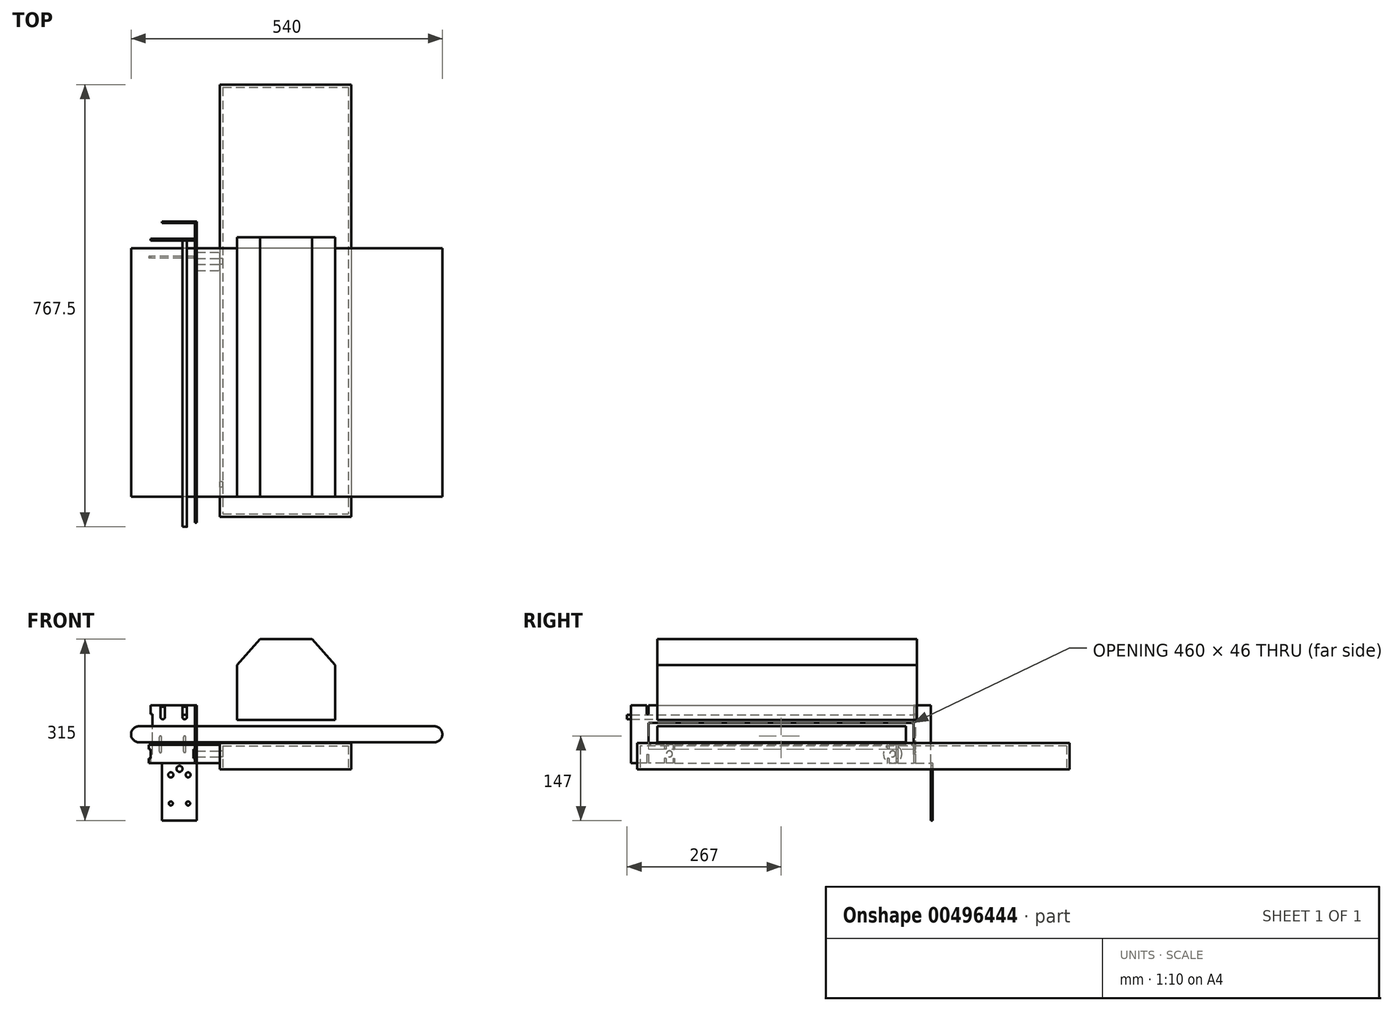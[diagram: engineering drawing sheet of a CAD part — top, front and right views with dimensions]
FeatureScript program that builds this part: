
annotation { "Feature Type Name" : "Feature", "Feature Type Description" : "" }
export const myFeature = defineFeature(function(context is Context, id is Id, definition is map)
    precondition{}
    {
        {
            var Q0;
            Q0=qCreatedBy(makeId("Front.planeOp"),FACE);
            var sketch = newSketch(context, id + "F0", { "sketchPlane" : qUnion([Q0])});
            skLineSegment(sketch, "E0.bottom", {"start": v(270, -14) * mm, "end": v(-270, -14) * mm});
            skLineSegment(sketch, "E0.top", {"start": v(270, 14) * mm, "end": v(-270, 14) * mm});
            skLineSegment(sketch, "E0.left", {"start": v(270, -14) * mm, "end": v(270, 14) * mm});
            skLineSegment(sketch, "E0.right", {"start": v(-270, -14) * mm, "end": v(-270, 14) * mm});
            skPoint(sketch, "E0.middle", {"position": v(0, 0) * mm});
            skSolve(sketch);
        }
        {
            var Q0;
            Q0 = qSketchRegion(id + "F0", true);
            extrude(context, id + "F1", {"entities" : qUnion([Q0]), "oppositeDirection" : true, "depth" : 431 * mm});
        }
        {
            var Q0;
            Q0=makeQuery(id+"F1.opExtrude","SWEPT_EDGE",EDGE,{"disambiguationData":[OSD([sQuery(id+"F0.wireOp",EDGE,"E0.top"),sQuery(id+"F0.wireOp",EDGE,"E0.right")])]});
            var Q1;
            Q1=makeQuery(id+"F1.opExtrude","SWEPT_EDGE",EDGE,{"disambiguationData":[OSD([sQuery(id+"F0.wireOp",EDGE,"E0.bottom"),sQuery(id+"F0.wireOp",EDGE,"E0.right")])]});
            var Q2;
            Q2=makeQuery(id+"F1.opExtrude","SWEPT_EDGE",EDGE,{"disambiguationData":[OSD([sQuery(id+"F0.wireOp",EDGE,"E0.top"),sQuery(id+"F0.wireOp",EDGE,"E0.left")])]});
            var Q3;
            Q3=makeQuery(id+"F1.opExtrude","SWEPT_EDGE",EDGE,{"disambiguationData":[OSD([sQuery(id+"F0.wireOp",EDGE,"E0.bottom"),sQuery(id+"F0.wireOp",EDGE,"E0.left")])]});
            fillet(context, id + "F2", {"entities" : qUnion([Q0, Q1, Q2, Q3]), "radius" : 14 * mm, "tangentPropagation" : true, "allowEdgeOverflow" : false});
        }
        {
            var Q0;
            Q0=makeQuery(id+"F1.opExtrude","CAP_FACE",FACE,{"disambiguationData":[OSD([sQuery(id+"F0.wireOp",EDGE,"E0.bottom"),sQuery(id+"F0.wireOp",EDGE,"E0.top"),sQuery(id+"F0.wireOp",EDGE,"E0.left"),sQuery(id+"F0.wireOp",EDGE,"E0.right")])],"isStart":true});
            var sketch = newSketch(context, id + "F3", { "sketchPlane" : qUnion([Q0])});
            skLineSegment(sketch, "E1.bottom", {"start": v(-116, -15) * mm, "end": v(112, -15) * mm});
            skLineSegment(sketch, "E1.top", {"start": v(-116, -61) * mm, "end": v(112, -61) * mm});
            skLineSegment(sketch, "E1.left", {"start": v(-116, -15) * mm, "end": v(-116, -61) * mm});
            skLineSegment(sketch, "E1.right", {"start": v(112, -15) * mm, "end": v(112, -61) * mm});
            skSolve(sketch);
        }
        {
            var Q0;
            Q0 = qSketchRegion(id + "F3", true);
            extrude(context, id + "F4", {"entities" : qUnion([Q0]), "oppositeDirection" : true, "depth" : 715 * mm, "hasSecondDirection" : true, "secondDirectionOppositeDirection" : false, "secondDirectionDepth" : 35 * mm});
        }
        {
            var Q0;
            Q0=qCreatedBy(makeId("Front.planeOp"),FACE);
            var sketch = newSketch(context, id + "F5", { "sketchPlane" : qUnion([Q0])});
            skLineSegment(sketch, "E2.bottom", {"start": v(-46.31, 165) * mm, "end": v(44.31, 165) * mm});
            skLineSegment(sketch, "E2.top", {"start": v(-86, 25) * mm, "end": v(84, 25) * mm});
            skLineSegment(sketch, "E2.left", {"start": v(-86, 120) * mm, "end": v(-86, 25) * mm});
            skLineSegment(sketch, "E2.right", {"start": v(84, 120) * mm, "end": v(84, 25) * mm});
            skLineSegment(sketch, "E3", {"start": v(-86, 120) * mm, "end": v(-46.31, 165) * mm});
            skLineSegment(sketch, "E4", {"start": v(44.31, 165) * mm, "end": v(84, 120) * mm});
            skPoint(sketch, "E5.orphan", {"position": v(84, 165) * mm});
            skSolve(sketch);
        }
        {
            var Q0;
            Q0 = qSketchRegion(id + "F5", true);
            extrude(context, id + "F6", {"entities" : qUnion([Q0]), "oppositeDirection" : true, "depth" : 450 * mm});
        }
        {
            var Q0;
            Q0=makeQuery(id+"F1.opExtrude","CAP_FACE",FACE,{"disambiguationData":[OSD([sQuery(id+"F0.wireOp",EDGE,"E0.bottom"),sQuery(id+"F0.wireOp",EDGE,"E0.top"),sQuery(id+"F0.wireOp",EDGE,"E0.left"),sQuery(id+"F0.wireOp",EDGE,"E0.right")])],"isStart":true});
            var sketch = newSketch(context, id + "F7", { "sketchPlane" : qUnion([Q0])});
            skCircle(sketch, "E6", {"center": v(-112.05, 32.23) * mm, "radius": 12.5 * mm});
            skCircle(sketch, "E7", {"center": v(-112.05, 32.23) * mm, "radius": 6 * mm});
            skSolve(sketch);
        }
        {
            var Q0;
            Q0=makeQuery(id+"F7.imprint","IMPRINT",FACE,{"disambiguationData":[TD([[makeQuery(id+"F7.imprint","IMPRINT",EDGE,{"derivedFrom":sQuery(id+"F7.wireOp",EDGE,"E6")}),1.0]])]});
            extrude(context, id + "F8", {"entities" : qUnion([Q0]), "oppositeDirection" : true, "depth" : 400 * mm});
        }
        {
            var Q0;
            Q0=makeQuery(id+"F4.opExtrude","SWEPT_FACE",FACE,{"disambiguationData":[OSD([sQuery(id+"F3.wireOp",EDGE,"E1.top")])]});
            shell(context, id + "F9", {"entities" : qUnion([Q0]), "thickness" : 5 * mm});
        }
        {
            var Q0;
            Q0=makeQuery(id+"F4.opExtrude","SWEPT_FACE",FACE,{"disambiguationData":[OSD([sQuery(id+"F3.wireOp",EDGE,"E1.left")])]});
            var sketch = newSketch(context, id + "F10", { "sketchPlane" : qUnion([Q0])});
            skCircle(sketch, "E8", {"center": v(-21, -34) * mm, "radius": 5 * mm});
            skCircle(sketch, "E9", {"center": v(-408, -34) * mm, "radius": 5 * mm});
            skSolve(sketch);
        }
        {
            var Q0;
            Q0 = qSketchRegion(id + "F10", true);
            var Q1;
            Q1=sQuery(id+"F10.wireOp",EDGE,"E8");
            extrude(context, id + "F11", {"entities" : qUnion([Q0]), "operationType" : NewBodyOperationType.REMOVE, "surfaceEntities" : qUnion([Q1]), "oppositeDirection" : true, "depth" : 5 * mm});
        }
        {
            var Q0;
            Q0=makeQuery(id+"F4.opExtrude","SWEPT_FACE",FACE,{"disambiguationData":[OSD([sQuery(id+"F3.wireOp",EDGE,"E1.left")])]});
            var sketch = newSketch(context, id + "F12", { "sketchPlane" : qUnion([Q0])});
            skCircle(sketch, "E10", {"center": v(-408, -34) * mm, "radius": 16 * mm});
            skCircle(sketch, "E11", {"center": v(-408, -34) * mm, "radius": 5 * mm});
            skSolve(sketch);
        }
        {
            var Q0;
            Q0 = qSketchRegion(id + "F12", true);
            extrude(context, id + "F13", {"entities" : qUnion([Q0]), "depth" : 40 * mm});
        }
        {
            var Q0;
            Q0=makeQuery(id+"F13.opExtrude","CAP_FACE",FACE,{"disambiguationData":[OSD([sQuery(id+"F12.wireOp",EDGE,"E10"),sQuery(id+"F12.wireOp",EDGE,"E11")])],"isStart":false});
            var sketch = newSketch(context, id + "F14", { "sketchPlane" : qUnion([Q0])});
            skLineSegment(sketch, "E12.bottom", {"start": v(-214.5, -18) * mm, "end": v(-30, -18) * mm});
            skLineSegment(sketch, "E12.top", {"start": v(-214.5, -50) * mm, "end": v(-30, -50) * mm});
            skLineSegment(sketch, "E12.right", {"start": v(-21, -18) * mm, "end": v(-21, -50) * mm, "construction": true});
            skLineSegment(sketch, "E13", {"start": v(-214.5, -34) * mm, "end": v(-21, -34) * mm, "construction": true});
            skLineSegment(sketch, "E14", {"start": v(45.55, -50) * mm, "end": v(45.55, 50) * mm});
            skLineSegment(sketch, "E15", {"start": v(15.5, 20) * mm, "end": v(15.5, -18) * mm});
            skLineSegment(sketch, "E16", {"start": v(-214.5, -50) * mm, "end": v(-214.5, -18) * mm, "construction": true});
            skPoint(sketch, "E16.endSnap0", {"position": v(-198.32, -18) * mm});
            skPoint(sketch, "E17.orphan", {"position": v(-214.5, -34) * mm});
            skPoint(sketch, "E18.orphan", {"position": v(-408, -34) * mm});
            skLineSegment(sketch, "E19.MirrorCS", {"start": v(-444.5, 20) * mm, "end": v(-444.5, -18) * mm});
            skLineSegment(sketch, "E20.MirrorCS", {"start": v(-474.55, -50) * mm, "end": v(-474.55, 50) * mm});
            skLineSegment(sketch, "E21.MirrorCS", {"start": v(-214.5, -50) * mm, "end": v(-399, -50) * mm});
            skLineSegment(sketch, "E22.MirrorCS", {"start": v(-214.5, -18) * mm, "end": v(-399, -18) * mm});
            skCircle(sketch, "E23", {"center": v(-408, -34) * mm, "radius": 5.25 * mm});
            skCircle(sketch, "E24", {"center": v(-21, -34) * mm, "radius": 5.25 * mm});
            skLineSegment(sketch, "E25", {"start": v(45.55, 50) * mm, "end": v(18.55, 50) * mm});
            skLineSegment(sketch, "E26", {"start": v(-444.5, 20) * mm, "end": v(15.5, 20) * mm});
            skLineSegment(sketch, "E27.top", {"start": v(-447.55, 35) * mm, "end": v(-444.5, 35) * mm});
            skLineSegment(sketch, "E27.left", {"start": v(-447.55, 50) * mm, "end": v(-447.55, 35) * mm});
            skLineSegment(sketch, "E27.right", {"start": v(-444.5, 50) * mm, "end": v(-444.5, 35) * mm});
            skLineSegment(sketch, "E28.trimOffspring", {"start": v(-447.55, 50) * mm, "end": v(-474.55, 50) * mm});
            skLineSegment(sketch, "E29.top", {"start": v(15.5, 35) * mm, "end": v(18.55, 35) * mm});
            skLineSegment(sketch, "E29.left", {"start": v(15.5, 50) * mm, "end": v(15.5, 35) * mm});
            skLineSegment(sketch, "E29.right", {"start": v(18.55, 50) * mm, "end": v(18.55, 35) * mm});
            skLineSegment(sketch, "E30.trimOffspring", {"start": v(15.5, 50) * mm, "end": v(-444.5, 50) * mm});
            skLineSegment(sketch, "E31.bottom", {"start": v(-447.55, -35) * mm, "end": v(-444.5, -35) * mm});
            skLineSegment(sketch, "E31.left", {"start": v(-447.55, -35) * mm, "end": v(-447.55, -50) * mm});
            skLineSegment(sketch, "E31.right", {"start": v(-444.5, -35) * mm, "end": v(-444.5, -50) * mm});
            skLineSegment(sketch, "E32.trimOffspring", {"start": v(-447.55, -50) * mm, "end": v(-474.55, -50) * mm});
            skLineSegment(sketch, "E33.bottom", {"start": v(18.55, -35) * mm, "end": v(15.5, -35) * mm});
            skLineSegment(sketch, "E33.left", {"start": v(18.55, -35) * mm, "end": v(18.55, -50) * mm});
            skLineSegment(sketch, "E33.right", {"start": v(15.5, -35) * mm, "end": v(15.5, -50) * mm});
            skLineSegment(sketch, "E34.trimOffspring", {"start": v(18.55, -50) * mm, "end": v(45.55, -50) * mm});
            skLineSegment(sketch, "E35.left", {"start": v(-417, -18) * mm, "end": v(-417, -26) * mm});
            skLineSegment(sketch, "E35.right", {"start": v(-414, -18) * mm, "end": v(-414, -26) * mm});
            skLineSegment(sketch, "E36", {"start": v(-414, -26) * mm, "end": v(-417, -26) * mm});
            skLineSegment(sketch, "E37", {"start": v(-414, -42) * mm, "end": v(-417, -42) * mm});
            skLineSegment(sketch, "E38.trimOffspring", {"start": v(-414, -42) * mm, "end": v(-414, -50) * mm});
            skLineSegment(sketch, "E39.trimOffspring", {"start": v(-417, -42) * mm, "end": v(-417, -50) * mm});
            skLineSegment(sketch, "E40.trimOffspring", {"start": v(-417, -18) * mm, "end": v(-444.5, -18) * mm});
            skLineSegment(sketch, "E41.trimOffspring", {"start": v(-417, -50) * mm, "end": v(-444.5, -50) * mm});
            skLineSegment(sketch, "E42.left", {"start": v(-402, -18) * mm, "end": v(-402, -26) * mm});
            skLineSegment(sketch, "E42.right", {"start": v(-399, -18) * mm, "end": v(-399, -26) * mm});
            skLineSegment(sketch, "E43", {"start": v(-402, -26) * mm, "end": v(-399, -26) * mm});
            skLineSegment(sketch, "E44", {"start": v(-402, -42) * mm, "end": v(-399, -42) * mm});
            skLineSegment(sketch, "E45.trimOffspring", {"start": v(-399, -42) * mm, "end": v(-399, -50) * mm});
            skLineSegment(sketch, "E46.trimOffspring", {"start": v(-402, -42) * mm, "end": v(-402, -50) * mm});
            skLineSegment(sketch, "E47.trimOffspring", {"start": v(-402, -18) * mm, "end": v(-414, -18) * mm});
            skLineSegment(sketch, "E48.trimOffspring", {"start": v(-402, -50) * mm, "end": v(-414, -50) * mm});
            skLineSegment(sketch, "E49.MirrorCS", {"start": v(-27, -26) * mm, "end": v(-30, -26) * mm});
            skLineSegment(sketch, "E50.MirrorCS", {"start": v(-27, -42) * mm, "end": v(-30, -42) * mm});
            skLineSegment(sketch, "E51.MirrorCS", {"start": v(-27, -18) * mm, "end": v(-15, -18) * mm});
            skLineSegment(sketch, "E52.MirrorCS", {"start": v(-15, -26) * mm, "end": v(-12, -26) * mm});
            skLineSegment(sketch, "E53.MirrorCS", {"start": v(-15, -42) * mm, "end": v(-12, -42) * mm});
            skLineSegment(sketch, "E54.MirrorCS", {"start": v(-12, -42) * mm, "end": v(-12, -50) * mm});
            skLineSegment(sketch, "E55.MirrorCS", {"start": v(-27, -50) * mm, "end": v(-15, -50) * mm});
            skLineSegment(sketch, "E56.MirrorCS", {"start": v(-30, -42) * mm, "end": v(-30, -50) * mm});
            skLineSegment(sketch, "E57.MirrorCS", {"start": v(-15, -42) * mm, "end": v(-15, -50) * mm});
            skLineSegment(sketch, "E58.MirrorCS", {"start": v(-12, -18) * mm, "end": v(-12, -26) * mm});
            skLineSegment(sketch, "E59.MirrorCS", {"start": v(-27, -42) * mm, "end": v(-27, -50) * mm});
            skLineSegment(sketch, "E60.MirrorCS", {"start": v(-15, -18) * mm, "end": v(-15, -26) * mm});
            skLineSegment(sketch, "E61.MirrorCS", {"start": v(-27, -18) * mm, "end": v(-27, -26) * mm});
            skLineSegment(sketch, "E62.MirrorCS", {"start": v(-30, -18) * mm, "end": v(-30, -26) * mm});
            skLineSegment(sketch, "E63.trimOffspring", {"start": v(-12, -18) * mm, "end": v(15.5, -18) * mm});
            skLineSegment(sketch, "E64.trimOffspring", {"start": v(-12, -50) * mm, "end": v(15.5, -50) * mm});
            skSolve(sketch);
        }
        {
            var Q0;
            {var subQ6=sQuery(id+"F14.wireOp",EDGE,"E12.bottom");Q0=makeQuery(id+"F14.imprint","IMPRINT",FACE,{"disambiguationData":[TD([[makeQuery(id+"F14.imprint","IMPRINT",EDGE,{"derivedFrom":subQ6}),-1.0]])]});}
            var Q1;
            Q1 = qSketchRegion(id + "F14", true);
            extrude(context, id + "F15", {"entities" : qUnion([Q0, Q1]), "depth" : 3 * mm});
        }
        {
            var Q0;
            Q0=makeQuery(id+"F15.opExtrude","SWEPT_FACE",FACE,{"disambiguationData":[OSD([sQuery(id+"F14.wireOp",EDGE,"E20.MirrorCS")])]});
            var sketch = newSketch(context, id + "F16", { "sketchPlane" : qUnion([Q0])});
            skLineSegment(sketch, "E65.bottom", {"start": v(156, -50) * mm, "end": v(216, -50) * mm});
            skLineSegment(sketch, "E65.top", {"start": v(156, -150) * mm, "end": v(216, -150) * mm});
            skLineSegment(sketch, "E65.left", {"start": v(156, -50) * mm, "end": v(156, -150) * mm});
            skLineSegment(sketch, "E65.right", {"start": v(216, -50) * mm, "end": v(216, -150) * mm});
            skCircle(sketch, "E66", {"center": v(186, -60) * mm, "radius": 5.25 * mm});
            skPoint(sketch, "E66.centerSnap0", {"position": v(186, -50) * mm});
            skCircle(sketch, "E67", {"center": v(171, -120) * mm, "radius": 3.5 * mm});
            skCircle(sketch, "E68", {"center": v(201, -120) * mm, "radius": 3.5 * mm});
            skLineSegment(sketch, "E69", {"start": v(201, -120) * mm, "end": v(171, -120) * mm, "construction": true});
            skCircle(sketch, "E70", {"center": v(171, -70.46) * mm, "radius": 4.31 * mm});
            skCircle(sketch, "E71", {"center": v(201, -70.46) * mm, "radius": 4.48 * mm});
            skLineSegment(sketch, "E72", {"start": v(201, -120) * mm, "end": v(201, -70.46) * mm, "construction": true});
            skLineSegment(sketch, "E73", {"start": v(201, -70.46) * mm, "end": v(171, -70.46) * mm, "construction": true});
            skLineSegment(sketch, "E74", {"start": v(171, -120) * mm, "end": v(171, -70.46) * mm, "construction": true});
            skSolve(sketch);
        }
        {
            var Q0;
            Q0 = qSketchRegion(id + "F16", true);
            extrude(context, id + "F17", {"entities" : qUnion([Q0]), "depth" : 3 * mm});
        }
        {
            var Q0;
            Q0=makeQuery(id+"F17.opExtrude","CAP_FACE",FACE,{"disambiguationData":[OSD([sQuery(id+"F16.wireOp",EDGE,"E65.bottom"),sQuery(id+"F16.wireOp",EDGE,"E65.top"),sQuery(id+"F16.wireOp",EDGE,"E65.left"),sQuery(id+"F16.wireOp",EDGE,"E65.right"),sQuery(id+"F16.wireOp",EDGE,"E66"),sQuery(id+"F16.wireOp",EDGE,"E67"),sQuery(id+"F16.wireOp",EDGE,"E68")])],"isStart":true});
            var sketch = newSketch(context, id + "F18", { "sketchPlane" : qUnion([Q0])});
            skCircle(sketch, "E75", {"center": v(-186, -60) * mm, "radius": 5.25 * mm});
            skCircle(sketch, "E76", {"center": v(-186, -60) * mm, "radius": 4.25 * mm});
            skSolve(sketch);
        }
        {
            var Q0;
            Q0 = qSketchRegion(id + "F18", true);
            extrude(context, id + "F19", {"entities" : qUnion([Q0]), "depth" : 540 * mm, "hasSecondDirection" : true, "secondDirectionOppositeDirection" : true, "secondDirectionDepth" : 20 * mm});
        }
        {
            var Q0;
            Q0=makeQuery(id+"F15.opExtrude","SWEPT_FACE",FACE,{"disambiguationData":[OSD([sQuery(id+"F14.wireOp",EDGE,"E27.right")])]});
            var sketch = newSketch(context, id + "F20", { "sketchPlane" : qUnion([Q0])});
            skLineSegment(sketch, "E77.bottom", {"start": v(156, 50) * mm, "end": v(236, 50) * mm});
            skLineSegment(sketch, "E77.top", {"start": v(156, -50) * mm, "end": v(236, -50) * mm});
            skLineSegment(sketch, "E77.left", {"start": v(156, 50) * mm, "end": v(156, 35) * mm});
            skLineSegment(sketch, "E77.right", {"start": v(236, 50) * mm, "end": v(236, 35) * mm});
            skLineSegment(sketch, "E78.bottom", {"start": v(156, 35) * mm, "end": v(159, 35) * mm});
            skLineSegment(sketch, "E78.right", {"start": v(159, 35) * mm, "end": v(159, -35) * mm});
            skLineSegment(sketch, "E79", {"start": v(233, -35) * mm, "end": v(233, 35) * mm});
            skLineSegment(sketch, "E80", {"start": v(233, 35) * mm, "end": v(236, 35) * mm});
            skPoint(sketch, "E80.endSnap0", {"position": v(236, 35) * mm});
            skLineSegment(sketch, "E81", {"start": v(233, -35) * mm, "end": v(236, -35) * mm});
            skLineSegment(sketch, "E82", {"start": v(236, -35) * mm, "end": v(236, -50) * mm});
            skLineSegment(sketch, "E83", {"start": v(159, -35) * mm, "end": v(156, -35) * mm});
            skLineSegment(sketch, "E84", {"start": v(156, -35) * mm, "end": v(156, -50) * mm});
            skLineSegment(sketch, "E85.bottom", {"start": v(172.98, 48) * mm, "end": v(181.03, 48) * mm});
            skLineSegment(sketch, "E85.left", {"start": v(172.98, 48) * mm, "end": v(172.98, 30) * mm});
            skLineSegment(sketch, "E85.right", {"start": v(181.03, 48) * mm, "end": v(181.03, 30) * mm});
            skLineSegment(sketch, "E86", {"start": v(177, 30) * mm, "end": v(177, 48) * mm, "construction": true});
            skArc(sketch, "E87", {"start": v(172.98, 30) * mm, "mid": v(177, 25.97) * mm, "end": v(181.03, 30) * mm});
            skCircle(sketch, "E88", {"center": v(177, 30) * mm, "radius": 14 * mm, "construction": true});
            skLineSegment(sketch, "E89.bottom", {"start": v(210.98, 48) * mm, "end": v(219.03, 48) * mm});
            skLineSegment(sketch, "E89.left", {"start": v(210.98, 48) * mm, "end": v(210.98, 30) * mm});
            skLineSegment(sketch, "E89.right", {"start": v(219.03, 48) * mm, "end": v(219.03, 30) * mm});
            skLineSegment(sketch, "E90", {"start": v(215, 30) * mm, "end": v(215, 48) * mm, "construction": true});
            skArc(sketch, "E91", {"start": v(210.98, 30) * mm, "mid": v(215, 25.97) * mm, "end": v(219.03, 30) * mm});
            skCircle(sketch, "E92", {"center": v(215, 30) * mm, "radius": 14 * mm, "construction": true});
            skLineSegment(sketch, "E93", {"start": v(177, -5) * mm, "end": v(177, -30) * mm, "construction": true});
            skPoint(sketch, "E93.startSnap0", {"position": v(177, 25.97) * mm});
            skLineSegment(sketch, "E94.bottom", {"start": v(179, -30) * mm, "end": v(175, -30) * mm, "construction": true});
            skLineSegment(sketch, "E94.top", {"start": v(179, -5) * mm, "end": v(175, -5) * mm, "construction": true});
            skLineSegment(sketch, "E94.left", {"start": v(179, -30) * mm, "end": v(179, -5) * mm});
            skLineSegment(sketch, "E94.right", {"start": v(175, -30) * mm, "end": v(175, -5) * mm});
            skPoint(sketch, "E94.middle", {"position": v(177, -17.5) * mm});
            skPoint(sketch, "E95.orphan", {"position": v(177, -9.5) * mm});
            skPoint(sketch, "E96.orphan", {"position": v(177, -25.5) * mm});
            skLineSegment(sketch, "E97", {"start": v(219, -5) * mm, "end": v(219, -30) * mm, "construction": true});
            skLineSegment(sketch, "E98.bottom", {"start": v(221, -30) * mm, "end": v(217, -30) * mm, "construction": true});
            skLineSegment(sketch, "E98.top", {"start": v(221, -5) * mm, "end": v(217, -5) * mm, "construction": true});
            skLineSegment(sketch, "E98.left", {"start": v(221, -30) * mm, "end": v(221, -5) * mm});
            skLineSegment(sketch, "E98.right", {"start": v(217, -30) * mm, "end": v(217, -5) * mm});
            skPoint(sketch, "E98.middle", {"position": v(219, -17.5) * mm});
            skPoint(sketch, "E99.orphan", {"position": v(219, -9.5) * mm});
            skPoint(sketch, "E100.orphan", {"position": v(219, -25.5) * mm});
            skArc(sketch, "E101", {"start": v(221, -5) * mm, "mid": v(219, -3) * mm, "end": v(217, -5) * mm});
            skArc(sketch, "E102", {"start": v(217, -30) * mm, "mid": v(219, -32) * mm, "end": v(221, -30) * mm});
            skArc(sketch, "E103", {"start": v(179, -5) * mm, "mid": v(177, -3) * mm, "end": v(175, -5) * mm});
            skArc(sketch, "E104", {"start": v(175, -30) * mm, "mid": v(177, -32) * mm, "end": v(179, -30) * mm});
            skSolve(sketch);
        }
        {
            var Q0;
            Q0 = qSketchRegion(id + "F20", true);
            extrude(context, id + "F21", {"entities" : qUnion([Q0]), "depth" : 3 * mm});
        }
        {
            var Q0;
            Q0=makeQuery(id+"F21.opExtrude","CAP_FACE",FACE,{"disambiguationData":[OSD([sQuery(id+"F20.wireOp",EDGE,"E77.bottom"),sQuery(id+"F20.wireOp",EDGE,"E77.top"),sQuery(id+"F20.wireOp",EDGE,"E77.left"),sQuery(id+"F20.wireOp",EDGE,"E77.right"),sQuery(id+"F20.wireOp",EDGE,"E78.bottom"),sQuery(id+"F20.wireOp",EDGE,"E78.right"),sQuery(id+"F20.wireOp",EDGE,"E79"),sQuery(id+"F20.wireOp",EDGE,"E80"),sQuery(id+"F20.wireOp",EDGE,"E81"),sQuery(id+"F20.wireOp",EDGE,"E82"),sQuery(id+"F20.wireOp",EDGE,"E83"),sQuery(id+"F20.wireOp",EDGE,"E84"),sQuery(id+"F20.wireOp",EDGE,"E85.bottom"),sQuery(id+"F20.wireOp",EDGE,"E85.left"),sQuery(id+"F20.wireOp",EDGE,"E85.right"),sQuery(id+"F20.wireOp",EDGE,"E87"),sQuery(id+"F20.wireOp",EDGE,"E89.bottom"),sQuery(id+"F20.wireOp",EDGE,"E89.left"),sQuery(id+"F20.wireOp",EDGE,"E89.right"),sQuery(id+"F20.wireOp",EDGE,"E91")])],"isStart":false});
            var sketch = newSketch(context, id + "F22", { "sketchPlane" : qUnion([Q0])});
            skCircle(sketch, "E105", {"center": v(177, 30) * mm, "radius": 4 * mm});
            skSolve(sketch);
        }
        {
            var Q0;
            Q0 = qSketchRegion(id + "F22", true);
            extrude(context, id + "F23", {"entities" : qUnion([Q0]), "oppositeDirection" : true, "depth" : 500 * mm});
        }
        {
            var Q0;
            Q0=makeQuery(id+"F15.opExtrude","SWEPT_FACE",FACE,{"disambiguationData":[OSD([sQuery(id+"F14.wireOp",EDGE,"E35.right")])]});
            var sketch = newSketch(context, id + "F24", { "sketchPlane" : qUnion([Q0])});
            skLineSegment(sketch, "E106.bottom", {"start": v(159, -18) * mm, "end": v(239, -18) * mm});
            skLineSegment(sketch, "E106.top", {"start": v(159.08, -50) * mm, "end": v(239, -50) * mm});
            skLineSegment(sketch, "E106.left", {"start": v(162, -26) * mm, "end": v(162, -42) * mm});
            skLineSegment(sketch, "E106.right", {"start": v(236, -26) * mm, "end": v(236, -42) * mm});
            skLineSegment(sketch, "E107", {"start": v(159, -18) * mm, "end": v(159, -26) * mm});
            skLineSegment(sketch, "E108", {"start": v(162, -26) * mm, "end": v(159, -26) * mm});
            skLineSegment(sketch, "E109", {"start": v(159.08, -50) * mm, "end": v(159.08, -42) * mm});
            skLineSegment(sketch, "E110", {"start": v(162, -42) * mm, "end": v(159.08, -42) * mm});
            skLineSegment(sketch, "E111", {"start": v(239, -18) * mm, "end": v(239, -26) * mm});
            skLineSegment(sketch, "E112", {"start": v(236, -26) * mm, "end": v(239, -26) * mm});
            skLineSegment(sketch, "E113", {"start": v(239, -50) * mm, "end": v(239, -42) * mm});
            skLineSegment(sketch, "E114", {"start": v(236, -42) * mm, "end": v(239, -42) * mm});
            skSolve(sketch);
        }
        {
            var Q0;
            Q0 = qSketchRegion(id + "F24", true);
            extrude(context, id + "F25", {"entities" : qUnion([Q0]), "depth" : 3 * mm});
        }
        {
            var Q0;
            Q0=makeQuery(id+"F8.opExtrude","SWEPT_BODY",BODY,{"disambiguationData":[OSD([sQuery(id+"F7.wireOp",EDGE,"E6"),sQuery(id+"F7.wireOp",EDGE,"E7")])]});
            deleteBodies(context, id + "F26", {"entities" : qUnion([Q0])});
        }
        {
            var Q0;
            Q0=makeQuery(id+"F19.opExtrude","SWEPT_BODY",BODY,{"disambiguationData":[OSD([sQuery(id+"F18.wireOp",EDGE,"E75"),sQuery(id+"F18.wireOp",EDGE,"E76")])]});
            deleteBodies(context, id + "F27", {"entities" : qUnion([Q0])});
        }
    });
